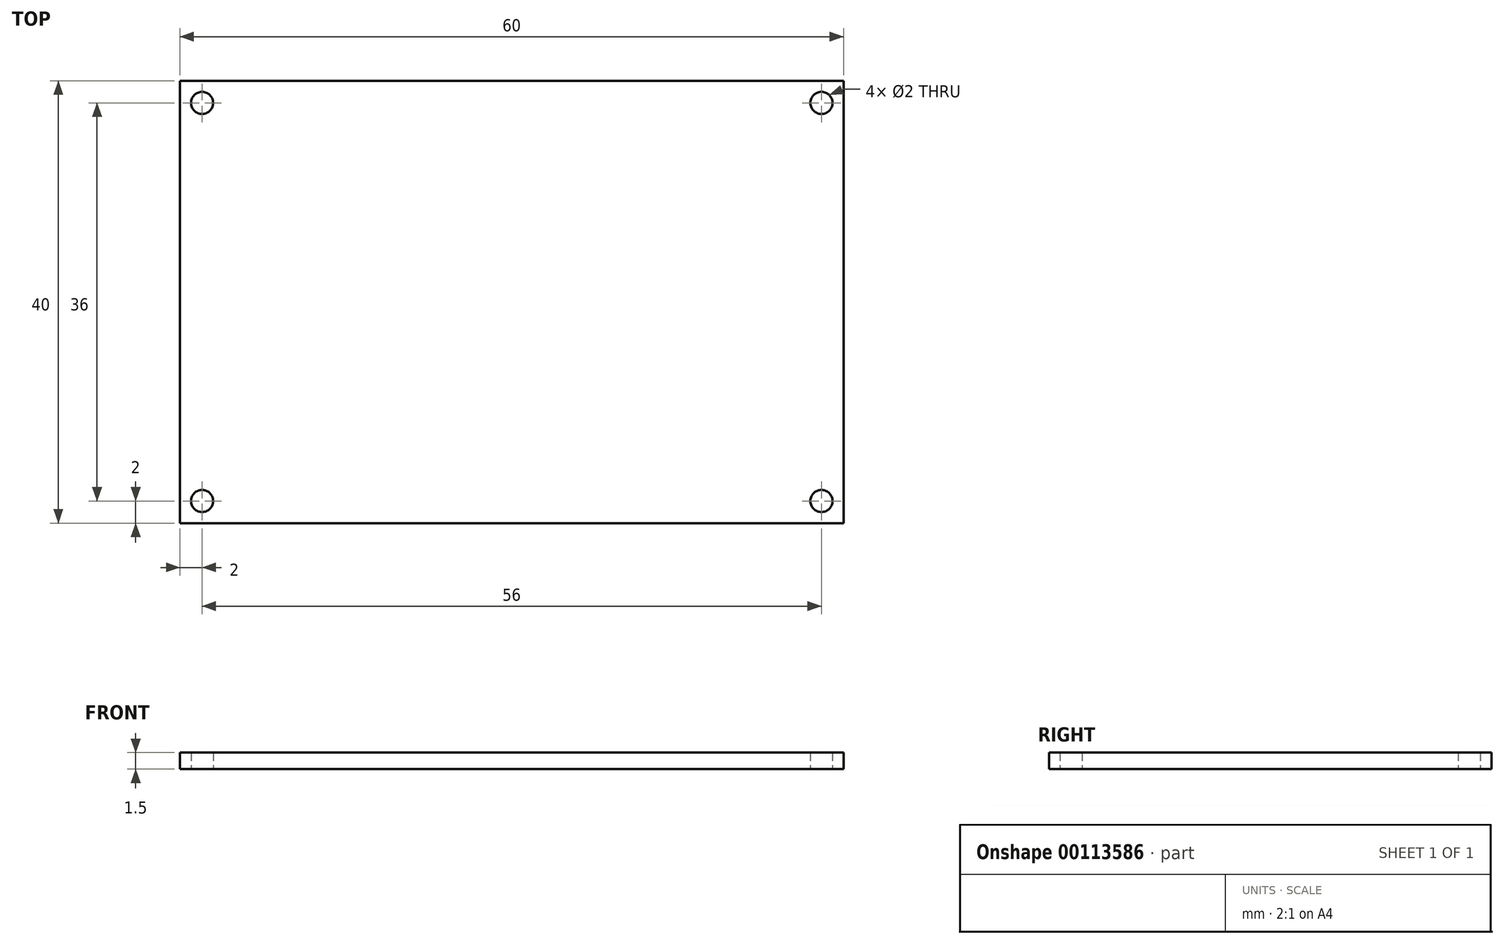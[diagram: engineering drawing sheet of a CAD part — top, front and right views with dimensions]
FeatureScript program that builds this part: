
annotation { "Feature Type Name" : "Feature", "Feature Type Description" : "" }
export const myFeature = defineFeature(function(context is Context, id is Id, definition is map)
    precondition{}
    {
        {
            assignVariable(context, id + "F0", {"name" : "pcb_thickness", "anyValue" : 1.5});
        }
        {
            var Q0;
            Q0=qCreatedBy(makeId("Top.planeOp"),FACE);
            var sketch = newSketch(context, id + "F1", { "sketchPlane" : qUnion([Q0])});
            skLineSegment(sketch, "E0.bottom", {"start": v(-30, 20) * mm, "end": v(30, 20) * mm});
            skLineSegment(sketch, "E0.top", {"start": v(-30, -20) * mm, "end": v(30, -20) * mm});
            skLineSegment(sketch, "E0.left", {"start": v(-30, 20) * mm, "end": v(-30, -20) * mm});
            skLineSegment(sketch, "E0.right", {"start": v(30, 20) * mm, "end": v(30, -20) * mm});
            skPoint(sketch, "E0.middle", {"position": v(0, 0) * mm});
            skSolve(sketch);
        }
        {
            var Q0;
            Q0 = qSketchRegion(id + "F1", true);
            extrude(context, id + "F2", {"entities" : qUnion([Q0]), "depth" : (getVariable(context, 'pcb_thickness')) * mm});
        }
        {
            var Q0;
            Q0=makeQuery(id+"F1.imprint","IMPRINT",FACE,{"disambiguationData":[TD([[makeQuery(id+"F1.imprint","IMPRINT",EDGE,{"derivedFrom":sQuery(id+"F1.wireOp",EDGE,"E0.bottom")}),-1.0]])]});
            var sketch = newSketch(context, id + "F3", { "sketchPlane" : qUnion([Q0])});
            skLineSegment(sketch, "E1.bottom", {"start": v(28, 18) * mm, "end": v(-28, 18) * mm, "construction": true});
            skLineSegment(sketch, "E1.top", {"start": v(28, -18) * mm, "end": v(-28, -18) * mm, "construction": true});
            skLineSegment(sketch, "E1.left", {"start": v(28, 18) * mm, "end": v(28, -18) * mm, "construction": true});
            skLineSegment(sketch, "E1.right", {"start": v(-28, 18) * mm, "end": v(-28, -18) * mm, "construction": true});
            skPoint(sketch, "E1.middle", {"position": v(0, 0) * mm});
            skCircle(sketch, "E2", {"center": v(-28, 18) * mm, "radius": 1 * mm});
            skCircle(sketch, "E3", {"center": v(28, 18) * mm, "radius": 1 * mm});
            skCircle(sketch, "E4", {"center": v(28, -18) * mm, "radius": 1 * mm});
            skCircle(sketch, "E5", {"center": v(-28, -18) * mm, "radius": 1 * mm});
            skSolve(sketch);
        }
        {
            var Q0;
            Q0 = qSketchRegion(id + "F3", true);
            var Q1;
            Q1=qCreatedBy(makeId("Front.planeOp"),FACE);
            extrude(context, id + "F4", {"entities" : qUnion([Q0]), "operationType" : NewBodyOperationType.REMOVE, "endBound" : BoundingType.UP_TO_NEXT, "endBoundEntityFace" : qUnion([Q1]), "depth" : 25 * mm});
        }
    });
